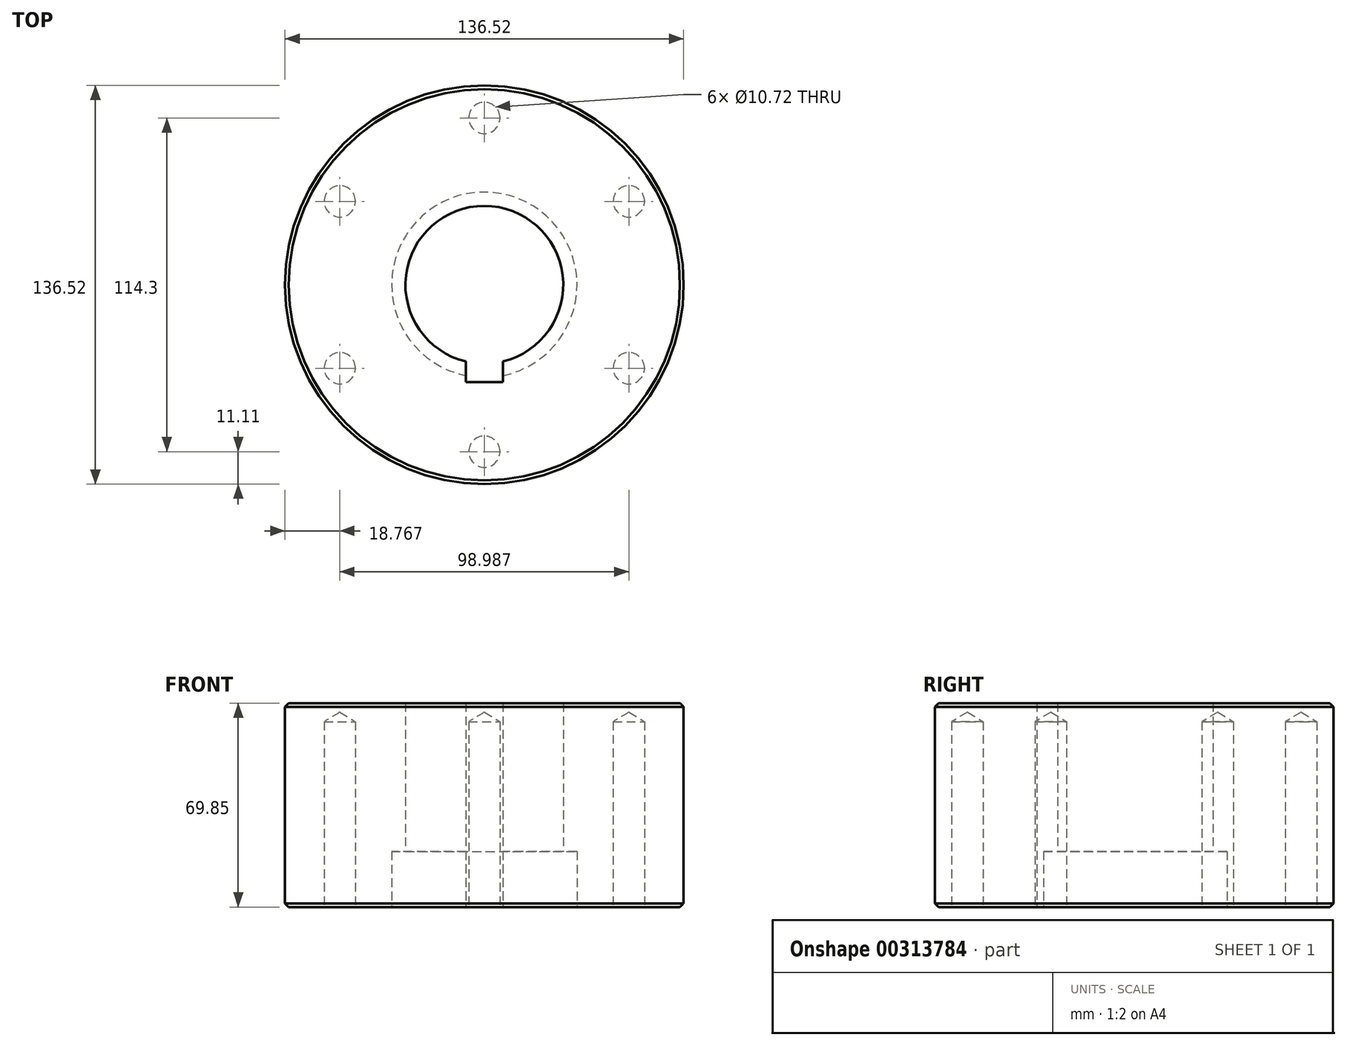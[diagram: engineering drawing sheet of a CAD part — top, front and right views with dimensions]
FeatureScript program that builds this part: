
annotation { "Feature Type Name" : "Feature", "Feature Type Description" : "" }
export const myFeature = defineFeature(function(context is Context, id is Id, definition is map)
    precondition{}
    {
        {
            var Q0;
            Q0=qCreatedBy(makeId("Top.planeOp"),FACE);
            var sketch = newSketch(context, id + "F0", { "sketchPlane" : qUnion([Q0])});
            skCircle(sketch, "E0", {"center": v(0, 0) * mm, "radius": 27.03 * mm});
            skCircle(sketch, "E1", {"center": v(0, 0) * mm, "radius": 68.26 * mm});
            skSolve(sketch);
        }
        {
            var Q0;
            Q0 = qSketchRegion(id + "F0", true);
            extrude(context, id + "F1", {"entities" : qUnion([Q0]), "depth" : 69.85 * mm});
        }
        {
            var Q0;
            Q0=makeQuery(id+"F1.opExtrude","CAP_FACE",FACE,{"disambiguationData":[OSD([sQuery(id+"F0.wireOp",EDGE,"E0"),sQuery(id+"F0.wireOp",EDGE,"E1")])],"isStart":true});
            var sketch = newSketch(context, id + "F2", { "sketchPlane" : qUnion([Q0])});
            skCircle(sketch, "E2", {"center": v(0, 57.15) * mm, "radius": 6.35 * mm});
            skCircle(sketch, "E3.1.0", {"center": v(-49.5, 28.58) * mm, "radius": 6.35 * mm});
            skCircle(sketch, "E3.2.0", {"center": v(-49.5, -28.57) * mm, "radius": 6.35 * mm});
            skCircle(sketch, "E3.3.0", {"center": v(0, -57.15) * mm, "radius": 6.35 * mm});
            skCircle(sketch, "E3.4.0", {"center": v(49.5, -28.58) * mm, "radius": 6.35 * mm});
            skCircle(sketch, "E3.5.0", {"center": v(49.5, 28.58) * mm, "radius": 6.35 * mm});
            skPoint(sketch, "E3.center", {"position": v(0, 0) * mm});
            skLineSegment(sketch, "E4", {"start": v(0, 0) * mm, "end": v(88.71, 0) * mm});
            skLineSegment(sketch, "E5", {"start": v(0, 0) * mm, "end": v(49.5, 28.58) * mm});
            skLineSegment(sketch, "E6", {"start": v(0, 0) * mm, "end": v(0, 57.15) * mm});
            skLineSegment(sketch, "E7", {"start": v(0, 0) * mm, "end": v(76.46, 44.15) * mm});
            skSolve(sketch);
        }
        {
            var Q0;
            Q0=makeQuery(id+"F1.opExtrude","CAP_FACE",FACE,{"disambiguationData":[OSD([sQuery(id+"F0.wireOp",EDGE,"E0"),sQuery(id+"F0.wireOp",EDGE,"E1")])],"isStart":true});
            var sketch = newSketch(context, id + "F3", { "sketchPlane" : qUnion([Q0])});
            skCircle(sketch, "E8", {"center": v(0, 0) * mm, "radius": 31.75 * mm});
            skSolve(sketch);
        }
        {
            var Q0;
            Q0 = qSketchRegion(id + "F3", true);
            extrude(context, id + "F4", {"entities" : qUnion([Q0]), "operationType" : NewBodyOperationType.REMOVE, "oppositeDirection" : true, "depth" : 19.05 * mm});
        }
        {
            var Q0;
            Q0=makeQuery(id+"F1.opExtrude","CAP_FACE",FACE,{"disambiguationData":[OSD([sQuery(id+"F0.wireOp",EDGE,"E0"),sQuery(id+"F0.wireOp",EDGE,"E1")])],"isStart":true});
            var sketch = newSketch(context, id + "F5", { "sketchPlane" : qUnion([Q0])});
            skLineSegment(sketch, "E9", {"start": v(-72.6, 0) * mm, "end": v(-72.6, 33.34) * mm});
            skLineSegment(sketch, "E10", {"start": v(-72.6, 33.34) * mm, "end": v(82.29, 33.34) * mm});
            skLineSegment(sketch, "E11.bottom", {"start": v(-6.35, 33.34) * mm, "end": v(6.35, 33.34) * mm});
            skLineSegment(sketch, "E11.left", {"start": v(-6.35, 33.34) * mm, "end": v(-6.35, 0) * mm});
            skLineSegment(sketch, "E11.right", {"start": v(6.35, 33.34) * mm, "end": v(6.35, 0) * mm});
            skPoint(sketch, "E11.middle", {"position": v(0, 0) * mm});
            skLineSegment(sketch, "E12", {"start": v(-6.35, 0) * mm, "end": v(6.35, 0) * mm});
            skPoint(sketch, "E13.orphan", {"position": v(-6.35, -33.34) * mm});
            skPoint(sketch, "E14.orphan", {"position": v(6.35, -33.34) * mm});
            skSolve(sketch);
        }
        {
            var Q0;
            Q0 = qSketchRegion(id + "F5", true);
            extrude(context, id + "F6", {"entities" : qUnion([Q0]), "operationType" : NewBodyOperationType.REMOVE, "endBound" : BoundingType.THROUGH_ALL, "oppositeDirection" : true, "depth" : 25.4 * mm});
        }
        {
            var Q0;
            Q0=makeQuery(id+"F1.opExtrude","CAP_EDGE",EDGE,{"disambiguationData":[OSD([sQuery(id+"F0.wireOp",EDGE,"E1")])],"isStart":false});
            var Q1;
            Q1=makeQuery(id+"F1.opExtrude","CAP_EDGE",EDGE,{"disambiguationData":[OSD([sQuery(id+"F0.wireOp",EDGE,"E1")])],"isStart":true});
            chamfer(context, id + "F7", {"entities" : qUnion([Q0, Q1]), "width" : 1.27 * mm, "tangentPropagation" : true});
        }
        {
            var Q0;
            Q0=sQuery(id+"F2.wireOp",VERTEX,"E2.center");
            var Q1;
            Q1=sQuery(id+"F2.wireOp",VERTEX,"E3.1.0.center");
            var Q2;
            Q2=sQuery(id+"F2.wireOp",VERTEX,"E3.5.0.center");
            var Q3;
            Q3=sQuery(id+"F2.wireOp",VERTEX,"E3.4.0.center");
            var Q4;
            Q4=sQuery(id+"F2.wireOp",VERTEX,"E3.3.0.center");
            var Q5;
            Q5=sQuery(id+"F2.wireOp",VERTEX,"E3.2.0.center");
            var Q6;
            Q6=makeQuery(id+"F1.opExtrude","SWEPT_BODY",BODY,{"disambiguationData":[OSD([sQuery(id+"F0.wireOp",EDGE,"E0"),sQuery(id+"F0.wireOp",EDGE,"E1")])]});
            hole(context, id + "F8", {"style" : HoleStyle.SIMPLE, "endStyle" : HoleEndStyle.BLIND, "standardTappedOrClearance" : lookupTablePath({ "standard" : "ANSI", "engagement" : "75%", "pitch" : "13 tpi", "size" : "1/2", "type" : "Tapped" }), "standardBlindInLast" : lookupTablePath({ "standard" : "ANSI", "engagement" : "75%", "pitch" : "13 tpi", "size" : "1/2", "type" : "Tapped" }), "holeDiameter" : 10.72 * mm, "showTappedDepth" : true, "holeDepth" : 63.5 * mm, "tappedDepth" : 57.64 * mm, "tapClearance" : 3, "startFromSketch" : true, "locations" : qUnion([Q0, Q1, Q2, Q3, Q4, Q5]), "scope" : qUnion([Q6]), "majorDiameter" : 12.7 * mm});
        }
    });
